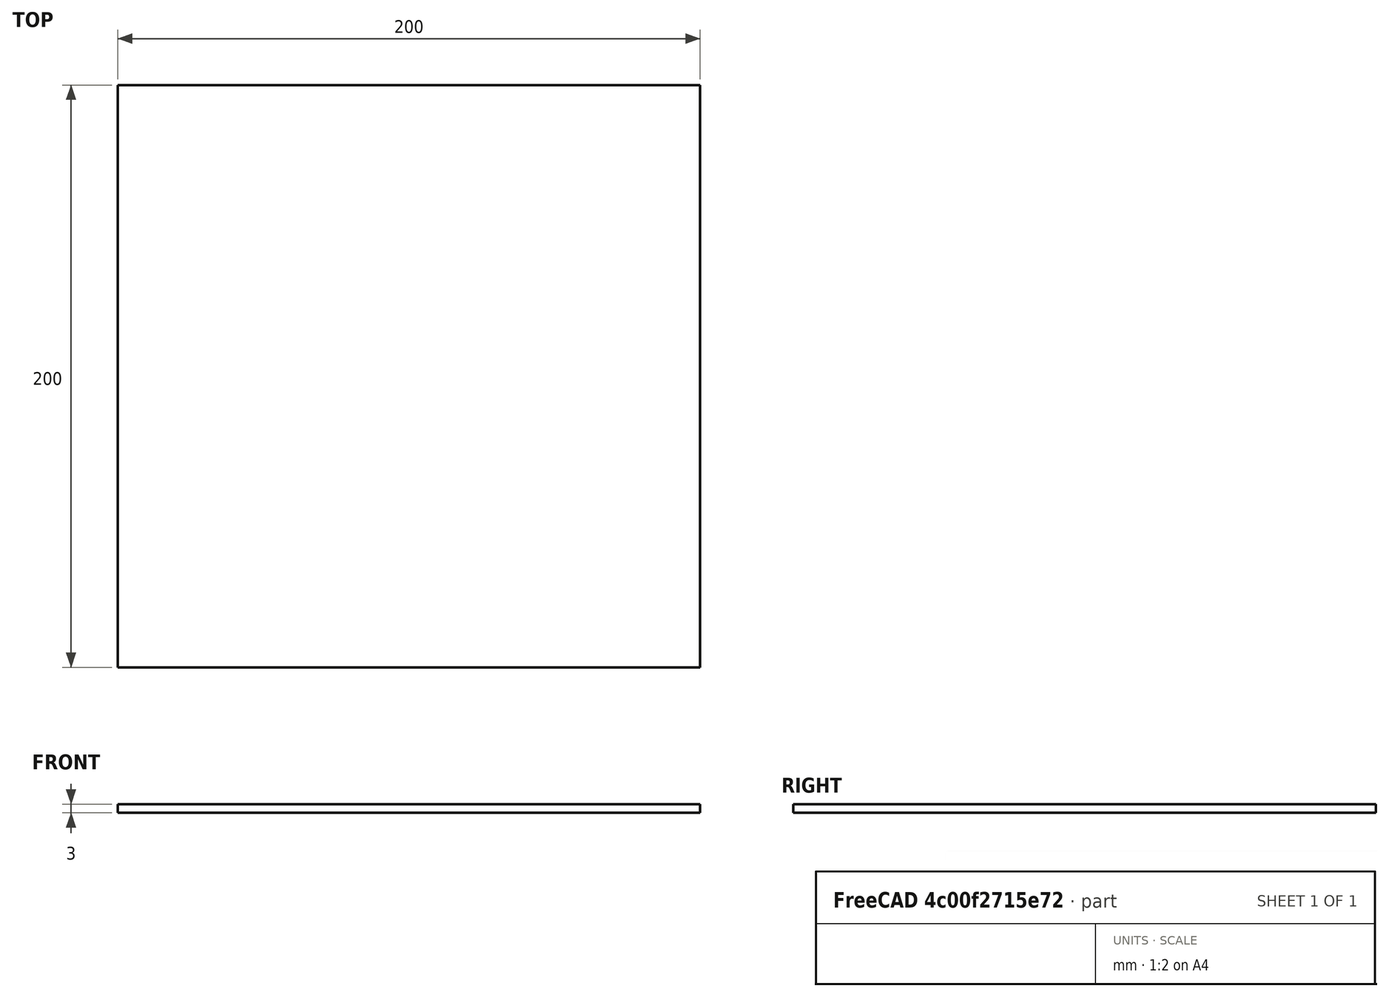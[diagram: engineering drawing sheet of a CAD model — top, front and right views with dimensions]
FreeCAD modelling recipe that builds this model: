
FCSTD DOCUMENT  (FreeCAD 0.18.4R)
Label: gripper-base
License: All rights reserved
LicenseURL: http://en.wikipedia.org/wiki/All_rights_reserved
objects: Sketcher::SketchObject×1, PartDesign::Pad×1, PartDesign::Body×1
note: 4 computed .brp shape members not serialized (recipe doc carries the construction recipe); baked Part::Feature solids carry a one-line shape summary decoded from their .brp

FEATURE [Sketcher::SketchObject] Sketch
  MapMode = 5
  Support = -> [XY_Plane]
  sketch-geometry (4):
    g0: LineSegment StartX=-100 StartY=100 StartZ=0 EndX=100 EndY=100 EndZ=0
    g1: LineSegment StartX=100 StartY=100 StartZ=0 EndX=100 EndY=-100 EndZ=0
    g2: LineSegment StartX=100 StartY=-100 StartZ=0 EndX=-100 EndY=-100 EndZ=0
    g3: LineSegment StartX=-100 StartY=-100 StartZ=0 EndX=-100 EndY=100 EndZ=0
  constraints (12):
    c: Coincident(g0,g1)
    c: Coincident(g1,g2)
    c: Coincident(g2,g3)
    c: Coincident(g3,g0)
    c: Horizontal(g0)
    c: Horizontal(g2)
    c: Vertical(g1)
    c: Vertical(g3)
    c: DistanceX(g0,g0) = 200
    c: Equal(g3,g0)
    c: DistanceX(g0,g-1) = 100
    c: DistanceY(g2,g-1) = 100
FEATURE [PartDesign::Pad] Pad
  Length = 3
  Length2 = 100
  Profile = -> Sketch
  Type = 0
FEATURE [PartDesign::Body] Body
  Group = -> [Sketch,Pad]
  Origin = -> Origin
  Tip = -> Pad
